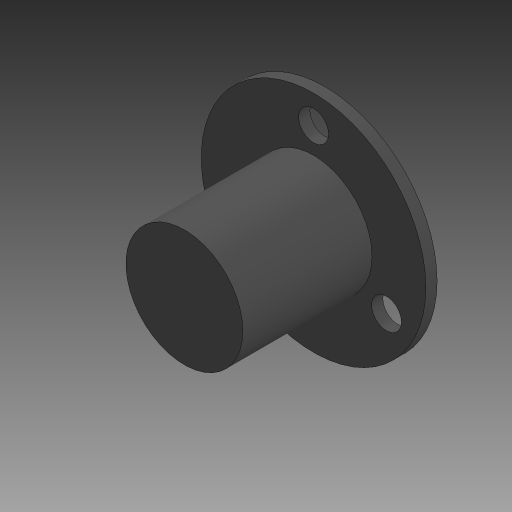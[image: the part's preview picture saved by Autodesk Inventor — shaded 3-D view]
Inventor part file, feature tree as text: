
AUTODESK INVENTOR PART (.ipt)
format: ipt  version: 2023 (Build 270158000, 158)  size: 123,904 bytes
history: native  units: mm
features: extrude x4, sketch x4, other x1
ambient origin geometry x8: Origin, YZ Plane, XZ Plane, XY Plane, X Axis, Y Axis, Z Axis, Center Point
bodies: Body1 (feature_tree)
feature tree (9):
  other  "Těleso1"
  extrude  "Vysunutí1"  Depth=24.0mm
  extrude  "Vysunutí2"  Depth=1.2mm TaperAngle=0.0deg
  extrude  "Vysunutí3"  Depth=18.0mm
  extrude  "Vysunutí4"  Depth=3.2mm
  sketch  "Náčrt1"
  sketch  "Náčrt2"
  sketch  "Náčrt3"
  sketch  "Náčrt4"
